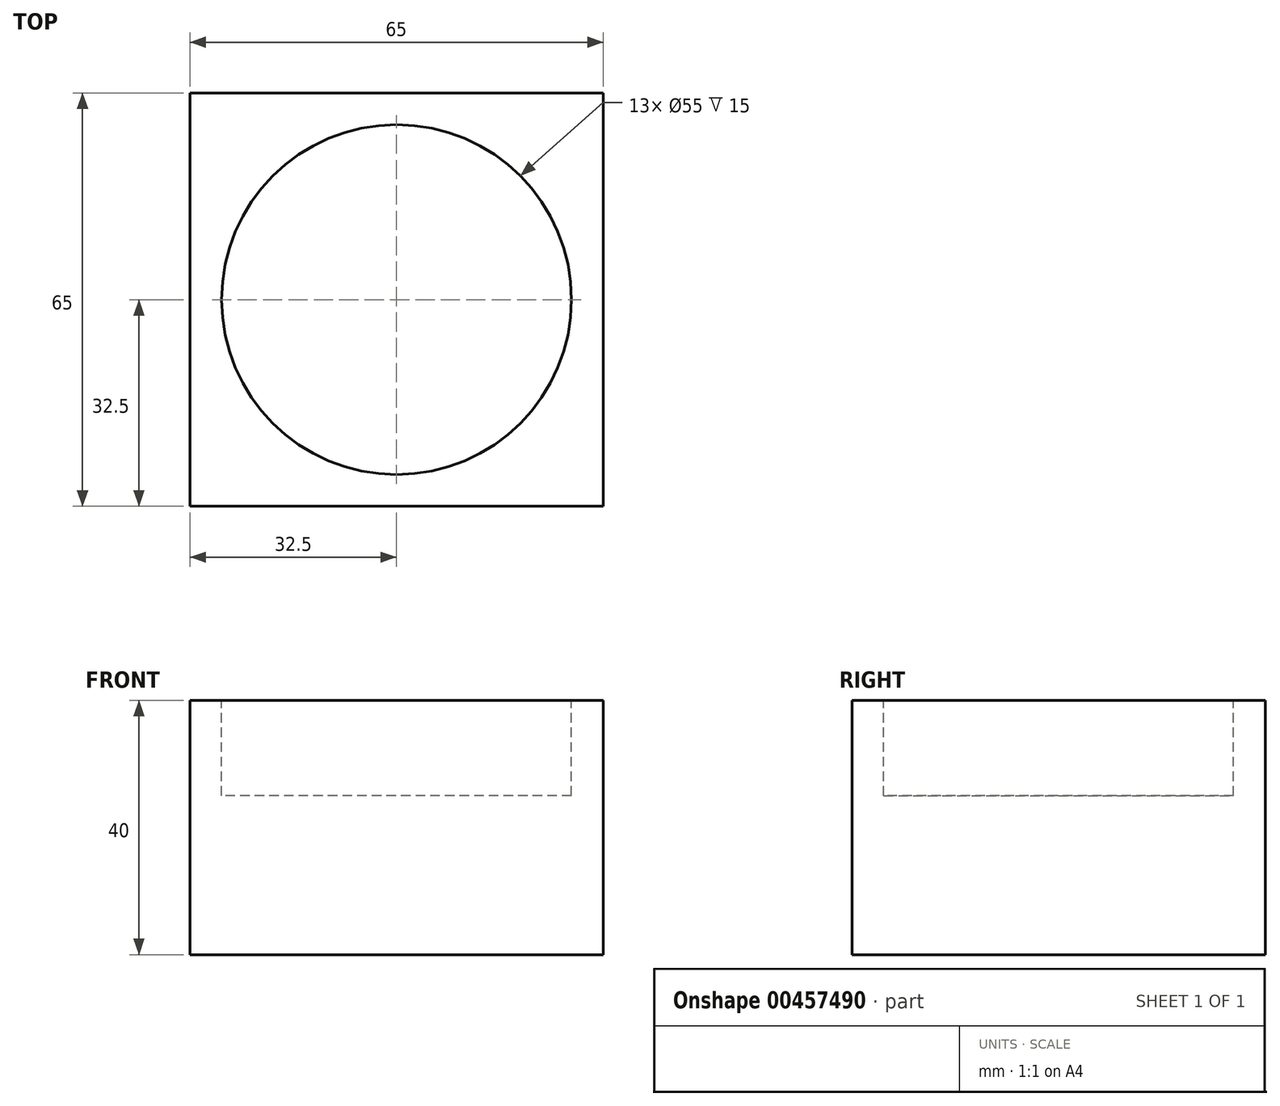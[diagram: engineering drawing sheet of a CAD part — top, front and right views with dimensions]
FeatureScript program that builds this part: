
annotation { "Feature Type Name" : "Feature", "Feature Type Description" : "" }
export const myFeature = defineFeature(function(context is Context, id is Id, definition is map)
    precondition{}
    {
        {
            var Q0;
            Q0=qCreatedBy(makeId("Top.planeOp"),FACE);
            var sketch = newSketch(context, id + "F0", { "sketchPlane" : qUnion([Q0])});
            skLineSegment(sketch, "E0.bottom", {"start": v(0, 0) * mm, "end": v(-65, 0) * mm});
            skLineSegment(sketch, "E0.top", {"start": v(0, -65) * mm, "end": v(-65, -65) * mm});
            skLineSegment(sketch, "E0.left", {"start": v(0, 0) * mm, "end": v(0, -65) * mm});
            skLineSegment(sketch, "E0.right", {"start": v(-65, 0) * mm, "end": v(-65, -65) * mm});
            skSolve(sketch);
        }
        {
            var Q0;
            Q0=makeQuery(id+"F0.imprint","IMPRINT",FACE,{"disambiguationData":[TD([[makeQuery(id+"F0.imprint","IMPRINT",EDGE,{"derivedFrom":sQuery(id+"F0.wireOp",EDGE,"E0.bottom")}),1.0]])]});
            extrude(context, id + "F1", {"entities" : qUnion([Q0]), "depth" : 40 * mm});
        }
        {
            var Q0;
            Q0=makeQuery(id+"F1.opExtrude","CAP_FACE",FACE,{"disambiguationData":[OSD([sQuery(id+"F0.wireOp",EDGE,"E0.bottom"),sQuery(id+"F0.wireOp",EDGE,"E0.top"),sQuery(id+"F0.wireOp",EDGE,"E0.left"),sQuery(id+"F0.wireOp",EDGE,"E0.right")])],"isStart":false});
            var sketch = newSketch(context, id + "F2", { "sketchPlane" : qUnion([Q0])});
            skLineSegment(sketch, "E1", {"start": v(-65, 0) * mm, "end": v(0, -65) * mm});
            skLineSegment(sketch, "E2", {"start": v(0, -65) * mm, "end": v(0, 0) * mm});
            skLineSegment(sketch, "E3", {"start": v(0, 0) * mm, "end": v(-65, -65) * mm});
            skCircle(sketch, "E4", {"center": v(-32.5, -32.5) * mm, "radius": 27.5 * mm});
            skSolve(sketch);
        }
        {
            var Q0;
            {var subQ0=sQuery(id+"F2.wireOp",EDGE,"E3");var subQ1=sQuery(id+"F2.wireOp",EDGE,"E1");var subQ2=makeQuery(id+"F2.imprint","INTERSECT",VERTEX,{"derivedFrom":[subQ1,subQ0]});Q0=makeQuery(id+"F2.imprint","IMPRINT",FACE,{"disambiguationData":[TD([[makeQuery(id+"F2.imprint","IMPRINT",EDGE,{"disambiguationData":[TD([[subQ2,-1.0]])],"derivedFrom":subQ1}),1.0]])]});}
            var Q1;
            {var subQ0=sQuery(id+"F2.wireOp",EDGE,"E4");var subQ1=sQuery(id+"F2.wireOp",EDGE,"E1");var subQ2=makeQuery(id+"F2.imprint","INTERSECT",VERTEX,{"disambiguationData":[OD(0.0)],"derivedFrom":[subQ1,subQ0]});Q1=makeQuery(id+"F2.imprint","IMPRINT",FACE,{"disambiguationData":[TD([[makeQuery(id+"F2.imprint","IMPRINT",EDGE,{"disambiguationData":[TD([[subQ2,-1.0]])],"derivedFrom":subQ1}),1.0]])]});}
            var Q2;
            {var subQ0=sQuery(id+"F2.wireOp",EDGE,"E4");var subQ1=sQuery(id+"F2.wireOp",EDGE,"E1");var subQ2=makeQuery(id+"F2.imprint","INTERSECT",VERTEX,{"disambiguationData":[OD(0.0)],"derivedFrom":[subQ1,subQ0]});Q2=makeQuery(id+"F2.imprint","IMPRINT",FACE,{"disambiguationData":[TD([[makeQuery(id+"F2.imprint","IMPRINT",EDGE,{"disambiguationData":[TD([[subQ2,-1.0]])],"derivedFrom":subQ1}),-1.0]])]});}
            var Q3;
            {var subQ0=sQuery(id+"F2.wireOp",EDGE,"E3");var subQ1=sQuery(id+"F2.wireOp",EDGE,"E1");var subQ2=makeQuery(id+"F2.imprint","INTERSECT",VERTEX,{"derivedFrom":[subQ1,subQ0]});Q3=makeQuery(id+"F2.imprint","IMPRINT",FACE,{"disambiguationData":[TD([[makeQuery(id+"F2.imprint","IMPRINT",EDGE,{"disambiguationData":[TD([[subQ2,-1.0]])],"derivedFrom":subQ1}),-1.0]])]});}
            extrude(context, id + "F3", {"entities" : qUnion([Q0, Q1, Q2, Q3]), "operationType" : NewBodyOperationType.REMOVE, "oppositeDirection" : true, "depth" : 15 * mm});
        }
    });
